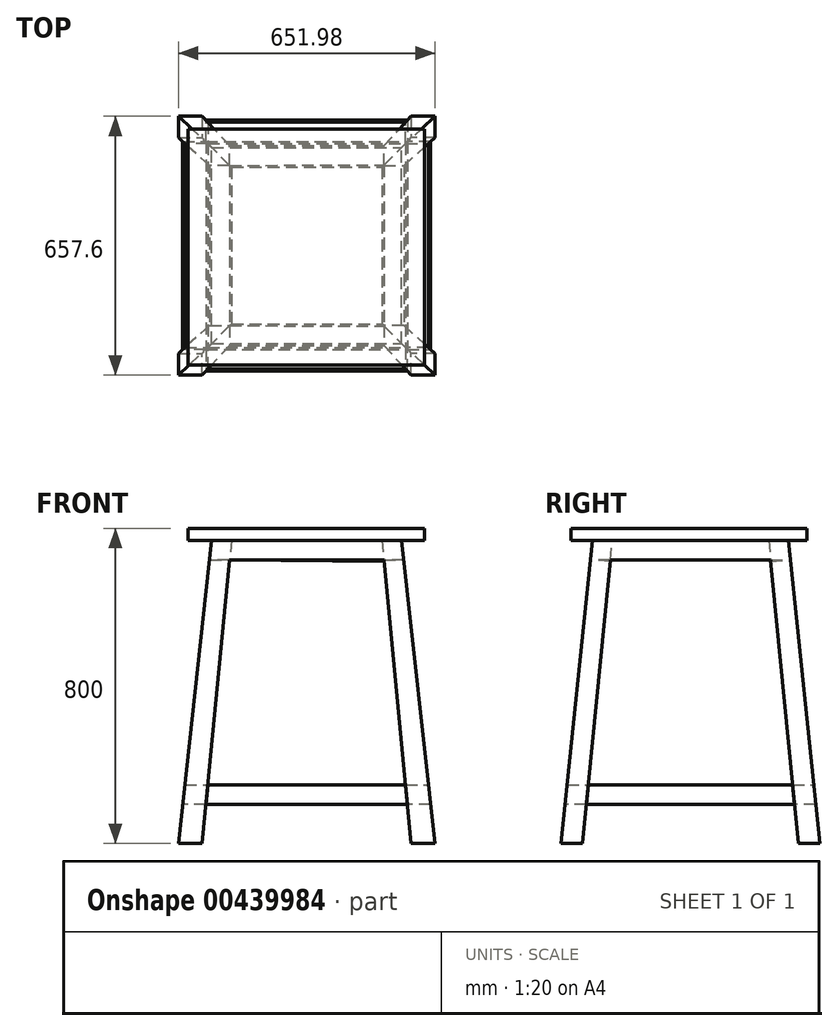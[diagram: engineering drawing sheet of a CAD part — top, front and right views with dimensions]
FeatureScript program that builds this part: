
annotation { "Feature Type Name" : "Feature", "Feature Type Description" : "" }
export const myFeature = defineFeature(function(context is Context, id is Id, definition is map)
    precondition{}
    {
        {
            var Q0;
            Q0=qCreatedBy(makeId("Top.planeOp"),FACE);
            var sketch = newSketch(context, id + "F0", { "sketchPlane" : qUnion([Q0])});
            skLineSegment(sketch, "E0.bottom", {"start": v(-301, 296.2) * mm, "end": v(299, 296.2) * mm});
            skLineSegment(sketch, "E0.top", {"start": v(-301, -303.8) * mm, "end": v(299, -303.8) * mm});
            skLineSegment(sketch, "E0.left", {"start": v(-301, 296.2) * mm, "end": v(-301, -303.8) * mm});
            skLineSegment(sketch, "E0.right", {"start": v(299, 296.2) * mm, "end": v(299, -303.8) * mm});
            skSolve(sketch);
        }
        {
            var Q0;
            Q0 = qSketchRegion(id + "F0", true);
            extrude(context, id + "F1", {"entities" : qUnion([Q0]), "depth" : 30 * mm});
        }
        {
            var Q0;
            Q0=qCreatedBy(makeId("Top.planeOp"),FACE);
            var sketch = newSketch(context, id + "F2", { "sketchPlane" : qUnion([Q0])});
            skLineSegment(sketch, "E1.bottom", {"start": v(-241.24, -248.9) * mm, "end": v(-191.24, -248.9) * mm});
            skLineSegment(sketch, "E1.top", {"start": v(-241.24, -198.9) * mm, "end": v(-191.24, -198.9) * mm});
            skLineSegment(sketch, "E1.left", {"start": v(-241.24, -248.9) * mm, "end": v(-241.24, -198.9) * mm});
            skLineSegment(sketch, "E1.right", {"start": v(-191.24, -248.9) * mm, "end": v(-191.24, -198.9) * mm});
            skSolve(sketch);
        }
        {
            var Q0;
            Q0=makeQuery(id+"F1.opExtrude","CAP_FACE",FACE,{"disambiguationData":[OSD([sQuery(id+"F0.wireOp",EDGE,"E0.bottom"),sQuery(id+"F0.wireOp",EDGE,"E0.top"),sQuery(id+"F0.wireOp",EDGE,"E0.left"),sQuery(id+"F0.wireOp",EDGE,"E0.right")])],"isStart":false});
            cPlane(context, id + "F3", {"entities" : qUnion([Q0]), "cplaneType" : CPlaneType.OFFSET, "offset" : 800 * mm, "oppositeDirection" : true, "width" : 150 * mm, "height" : 150 * mm});
        }
        {
            var Q0;
            Q0=qCreatedBy(id+"F3.planeOp",FACE);
            var sketch = newSketch(context, id + "F4", { "sketchPlane" : qUnion([Q0])});
            skLineSegment(sketch, "E2.bottom", {"start": v(-326, -328.8) * mm, "end": v(-265.45, -328.8) * mm});
            skLineSegment(sketch, "E2.top", {"start": v(-326, -273.84) * mm, "end": v(-265.45, -273.84) * mm});
            skLineSegment(sketch, "E2.left", {"start": v(-326, -328.8) * mm, "end": v(-326, -273.84) * mm});
            skLineSegment(sketch, "E2.right", {"start": v(-265.45, -328.8) * mm, "end": v(-265.45, -273.84) * mm});
            skSolve(sketch);
        }
        {
            var Q1;
            Q1=makeQuery(id+"F2.imprint","IMPRINT",FACE,{"disambiguationData":[TD([[makeQuery(id+"F2.imprint","IMPRINT",EDGE,{"derivedFrom":sQuery(id+"F2.wireOp",EDGE,"E1.bottom")}),1.0]])]});
            var Q2;
            Q2=makeQuery(id+"F4.imprint","IMPRINT",FACE,{"disambiguationData":[TD([[makeQuery(id+"F4.imprint","IMPRINT",EDGE,{"derivedFrom":sQuery(id+"F4.wireOp",EDGE,"E2.bottom")}),1.0]])]});
            loft(context, id + "F5", {"sheetProfilesArray" : [{ "sheetProfileEntities" : qUnion([Q1]) }, { "sheetProfileEntities" : qUnion([Q2]) }]});
        }
        {
            var Q0;
            Q0=makeQuery(id+"F5.opLoft","SWEPT_BODY",BODY,{"disambiguationData":[OSD([makeQuery(id+"F2.imprint","IMPRINT",FACE,{"disambiguationData":[TD([[makeQuery(id+"F2.imprint","IMPRINT",EDGE,{"derivedFrom":sQuery(id+"F2.wireOp",EDGE,"E1.bottom")}),1.0]])]}),makeQuery(id+"F4.imprint","IMPRINT",FACE,{"disambiguationData":[TD([[makeQuery(id+"F4.imprint","IMPRINT",EDGE,{"derivedFrom":sQuery(id+"F4.wireOp",EDGE,"E2.bottom")}),1.0]])]})])]});
            var Q1;
            Q1=qCreatedBy(makeId("Right.planeOp"),FACE);
            mirror(context, id + "F6", {"entities" : qUnion([Q0]), "mirrorPlane" : qUnion([Q1])});
        }
        {
            var Q0;
            Q0=makeQuery(id+"F6.opPattern","COPY",BODY,{"derivedFrom":makeQuery(id+"F5.opLoft","SWEPT_BODY",BODY,{"disambiguationData":[OSD([makeQuery(id+"F2.imprint","IMPRINT",FACE,{"disambiguationData":[TD([[makeQuery(id+"F2.imprint","IMPRINT",EDGE,{"derivedFrom":sQuery(id+"F2.wireOp",EDGE,"E1.bottom")}),1.0]])]}),makeQuery(id+"F4.imprint","IMPRINT",FACE,{"disambiguationData":[TD([[makeQuery(id+"F4.imprint","IMPRINT",EDGE,{"derivedFrom":sQuery(id+"F4.wireOp",EDGE,"E2.bottom")}),1.0]])]})])]}),"instanceName":"1"});
            var Q1;
            Q1=makeQuery(id+"F5.opLoft","SWEPT_BODY",BODY,{"disambiguationData":[OSD([makeQuery(id+"F2.imprint","IMPRINT",FACE,{"disambiguationData":[TD([[makeQuery(id+"F2.imprint","IMPRINT",EDGE,{"derivedFrom":sQuery(id+"F2.wireOp",EDGE,"E1.bottom")}),1.0]])]}),makeQuery(id+"F4.imprint","IMPRINT",FACE,{"disambiguationData":[TD([[makeQuery(id+"F4.imprint","IMPRINT",EDGE,{"derivedFrom":sQuery(id+"F4.wireOp",EDGE,"E2.bottom")}),1.0]])]})])]});
            var Q2;
            Q2=qCreatedBy(makeId("Front.planeOp"),FACE);
            mirror(context, id + "F7", {"operationType" : NewBodyOperationType.ADD, "entities" : qUnion([Q0, Q1]), "mirrorPlane" : qUnion([Q2])});
        }
        {
            var Q0;
            Q0=makeQuery(id+"F7.opPattern","COPY",FACE,{"derivedFrom":makeQuery(id+"F6.opPattern","COPY",FACE,{"derivedFrom":makeQuery(id+"F5.opLoft","SWEPT_FACE",FACE,{"disambiguationData":[OSD([sQuery(id+"F2.wireOp",EDGE,"E1.bottom"),sQuery(id+"F2.wireOp",EDGE,"E1.top"),sQuery(id+"F2.wireOp",EDGE,"E1.right"),sQuery(id+"F4.wireOp",EDGE,"E2.bottom"),sQuery(id+"F4.wireOp",EDGE,"E2.top"),sQuery(id+"F4.wireOp",EDGE,"E2.right")])]}),"instanceName":"1"}),"instanceName":"1"});
            var sketch = newSketch(context, id + "F8", { "sketchPlane" : qUnion([Q0])});
            skLineSegment(sketch, "E3", {"start": v(-318.47, -691.91) * mm, "end": v(-264.15, -691.91) * mm});
            skLineSegment(sketch, "E4", {"start": v(-264.15, -691.91) * mm, "end": v(-259.33, -642.18) * mm});
            skLineSegment(sketch, "E5", {"start": v(-259.33, -642.18) * mm, "end": v(-313.34, -642.18) * mm});
            skLineSegment(sketch, "E6", {"start": v(-313.34, -642.18) * mm, "end": v(-318.47, -691.91) * mm});
            skSolve(sketch);
        }
        {
            var Q0;
            Q0=makeQuery(id+"F7.opPattern","COPY",FACE,{"derivedFrom":makeQuery(id+"F5.opLoft","SWEPT_FACE",FACE,{"disambiguationData":[OSD([sQuery(id+"F2.wireOp",EDGE,"E1.bottom"),sQuery(id+"F2.wireOp",EDGE,"E1.top"),sQuery(id+"F2.wireOp",EDGE,"E1.right"),sQuery(id+"F4.wireOp",EDGE,"E2.bottom"),sQuery(id+"F4.wireOp",EDGE,"E2.top"),sQuery(id+"F4.wireOp",EDGE,"E2.right")])]}),"instanceName":"1"});
            var sketch = newSketch(context, id + "F9", { "sketchPlane" : qUnion([Q0])});
            skLineSegment(sketch, "E7", {"start": v(264.15, -691.91) * mm, "end": v(318.47, -691.91) * mm});
            skLineSegment(sketch, "E8", {"start": v(318.47, -691.91) * mm, "end": v(313.34, -642.18) * mm});
            skLineSegment(sketch, "E9", {"start": v(313.34, -642.18) * mm, "end": v(259.33, -642.18) * mm});
            skLineSegment(sketch, "E10", {"start": v(259.33, -642.18) * mm, "end": v(264.15, -691.91) * mm});
            skSolve(sketch);
        }
        {
            var Q1;
            Q1=makeQuery(id+"F9.imprint","IMPRINT",FACE,{"disambiguationData":[TD([[makeQuery(id+"F9.imprint","IMPRINT",EDGE,{"derivedFrom":sQuery(id+"F9.wireOp",EDGE,"E7")}),1.0]])]});
            var Q2;
            Q2=makeQuery(id+"F8.imprint","IMPRINT",FACE,{"disambiguationData":[TD([[makeQuery(id+"F8.imprint","IMPRINT",EDGE,{"derivedFrom":sQuery(id+"F8.wireOp",EDGE,"E3")}),1.0]])]});
            loft(context, id + "F10", {"sheetProfilesArray" : [{ "sheetProfileEntities" : qUnion([Q1]) }, { "sheetProfileEntities" : qUnion([Q2]) }]});
        }
        {
            var Q0;
            Q0=makeQuery(id+"F10.opLoft","SWEPT_BODY",BODY,{"disambiguationData":[OSD([makeQuery(id+"F8.imprint","IMPRINT",FACE,{"disambiguationData":[TD([[makeQuery(id+"F8.imprint","IMPRINT",EDGE,{"derivedFrom":sQuery(id+"F8.wireOp",EDGE,"E3")}),1.0]])]}),makeQuery(id+"F9.imprint","IMPRINT",FACE,{"disambiguationData":[TD([[makeQuery(id+"F9.imprint","IMPRINT",EDGE,{"derivedFrom":sQuery(id+"F9.wireOp",EDGE,"E7")}),1.0]])]})])]});
            var Q1;
            Q1=qCreatedBy(makeId("Front.planeOp"),FACE);
            mirror(context, id + "F11", {"entities" : qUnion([Q0]), "mirrorPlane" : qUnion([Q1])});
        }
        {
            var Q0;
            Q0=makeQuery(id+"F5.opLoft","SWEPT_FACE",FACE,{"disambiguationData":[OSD([sQuery(id+"F2.wireOp",EDGE,"E1.top"),sQuery(id+"F2.wireOp",EDGE,"E1.left"),sQuery(id+"F2.wireOp",EDGE,"E1.right"),sQuery(id+"F4.wireOp",EDGE,"E2.top"),sQuery(id+"F4.wireOp",EDGE,"E2.left"),sQuery(id+"F4.wireOp",EDGE,"E2.right")])]});
            var sketch = newSketch(context, id + "F12", { "sketchPlane" : qUnion([Q0])});
            skLineSegment(sketch, "E11", {"start": v(255.85, -692.9) * mm, "end": v(315.04, -692.9) * mm});
            skLineSegment(sketch, "E12", {"start": v(315.04, -692.9) * mm, "end": v(309.6, -643.2) * mm});
            skLineSegment(sketch, "E13", {"start": v(309.6, -643.2) * mm, "end": v(251.09, -643.2) * mm});
            skLineSegment(sketch, "E14", {"start": v(251.09, -643.2) * mm, "end": v(255.85, -692.9) * mm});
            skSolve(sketch);
        }
        {
            var Q0;
            Q0=makeQuery(id+"F7.opPattern","COPY",FACE,{"derivedFrom":makeQuery(id+"F5.opLoft","SWEPT_FACE",FACE,{"disambiguationData":[OSD([sQuery(id+"F2.wireOp",EDGE,"E1.top"),sQuery(id+"F2.wireOp",EDGE,"E1.left"),sQuery(id+"F2.wireOp",EDGE,"E1.right"),sQuery(id+"F4.wireOp",EDGE,"E2.top"),sQuery(id+"F4.wireOp",EDGE,"E2.left"),sQuery(id+"F4.wireOp",EDGE,"E2.right")])]}),"instanceName":"1"});
            var sketch = newSketch(context, id + "F13", { "sketchPlane" : qUnion([Q0])});
            skLineSegment(sketch, "E15", {"start": v(-251.09, -643.2) * mm, "end": v(-309.6, -643.2) * mm});
            skLineSegment(sketch, "E16", {"start": v(-309.6, -643.2) * mm, "end": v(-315.04, -692.9) * mm});
            skLineSegment(sketch, "E17", {"start": v(-315.04, -692.9) * mm, "end": v(-255.85, -692.9) * mm});
            skLineSegment(sketch, "E18", {"start": v(-255.85, -692.9) * mm, "end": v(-251.09, -643.2) * mm});
            skSolve(sketch);
        }
        {
            var Q1;
            Q1=makeQuery(id+"F13.imprint","IMPRINT",FACE,{"disambiguationData":[TD([[makeQuery(id+"F13.imprint","IMPRINT",EDGE,{"derivedFrom":sQuery(id+"F13.wireOp",EDGE,"E15")}),1.0]])]});
            var Q2;
            Q2=makeQuery(id+"F12.imprint","IMPRINT",FACE,{"disambiguationData":[TD([[makeQuery(id+"F12.imprint","IMPRINT",EDGE,{"derivedFrom":sQuery(id+"F12.wireOp",EDGE,"E11")}),1.0]])]});
            loft(context, id + "F14", {"sheetProfilesArray" : [{ "sheetProfileEntities" : qUnion([Q1]) }, { "sheetProfileEntities" : qUnion([Q2]) }]});
        }
        {
            var Q0;
            Q0=makeQuery(id+"F14.opLoft","SWEPT_BODY",BODY,{"disambiguationData":[OSD([makeQuery(id+"F12.imprint","IMPRINT",FACE,{"disambiguationData":[TD([[makeQuery(id+"F12.imprint","IMPRINT",EDGE,{"derivedFrom":sQuery(id+"F12.wireOp",EDGE,"E11")}),1.0]])]}),makeQuery(id+"F13.imprint","IMPRINT",FACE,{"disambiguationData":[TD([[makeQuery(id+"F13.imprint","IMPRINT",EDGE,{"derivedFrom":sQuery(id+"F13.wireOp",EDGE,"E15")}),1.0]])]})])]});
            var Q1;
            Q1=qCreatedBy(makeId("Right.planeOp"),FACE);
            mirror(context, id + "F15", {"entities" : qUnion([Q0]), "mirrorPlane" : qUnion([Q1])});
        }
        {
            var Q0;
            Q0=makeQuery(id+"F7.opPattern","COPY",FACE,{"derivedFrom":makeQuery(id+"F6.opPattern","COPY",FACE,{"derivedFrom":makeQuery(id+"F5.opLoft","SWEPT_FACE",FACE,{"disambiguationData":[OSD([sQuery(id+"F2.wireOp",EDGE,"E1.bottom"),sQuery(id+"F2.wireOp",EDGE,"E1.top"),sQuery(id+"F2.wireOp",EDGE,"E1.right"),sQuery(id+"F4.wireOp",EDGE,"E2.bottom"),sQuery(id+"F4.wireOp",EDGE,"E2.top"),sQuery(id+"F4.wireOp",EDGE,"E2.right")])]}),"instanceName":"1"}),"instanceName":"1"});
            var sketch = newSketch(context, id + "F16", { "sketchPlane" : qUnion([Q0])});
            skLineSegment(sketch, "E19", {"start": v(-248.9, -18.35) * mm, "end": v(-198.9, -18.35) * mm});
            skLineSegment(sketch, "E20", {"start": v(-198.9, -18.35) * mm, "end": v(-204.18, -72.91) * mm});
            skLineSegment(sketch, "E21", {"start": v(-204.18, -72.91) * mm, "end": v(-254.03, -68.08) * mm});
            skLineSegment(sketch, "E22", {"start": v(-254.03, -68.08) * mm, "end": v(-248.9, -18.35) * mm});
            skSolve(sketch);
        }
        {
            var Q0;
            Q0=makeQuery(id+"F7.opPattern","COPY",FACE,{"derivedFrom":makeQuery(id+"F5.opLoft","SWEPT_FACE",FACE,{"disambiguationData":[OSD([sQuery(id+"F2.wireOp",EDGE,"E1.bottom"),sQuery(id+"F2.wireOp",EDGE,"E1.top"),sQuery(id+"F2.wireOp",EDGE,"E1.right"),sQuery(id+"F4.wireOp",EDGE,"E2.bottom"),sQuery(id+"F4.wireOp",EDGE,"E2.top"),sQuery(id+"F4.wireOp",EDGE,"E2.right")])]}),"instanceName":"1"});
            var sketch = newSketch(context, id + "F17", { "sketchPlane" : qUnion([Q0])});
            skLineSegment(sketch, "E23", {"start": v(248.9, -18.35) * mm, "end": v(198.9, -18.35) * mm});
            skLineSegment(sketch, "E24", {"start": v(198.9, -18.35) * mm, "end": v(203.71, -68.08) * mm});
            skLineSegment(sketch, "E25", {"start": v(203.71, -68.08) * mm, "end": v(254.03, -68.08) * mm});
            skLineSegment(sketch, "E26", {"start": v(254.03, -68.08) * mm, "end": v(248.9, -18.35) * mm});
            skSolve(sketch);
        }
        {
            var Q1;
            Q1=makeQuery(id+"F17.imprint","IMPRINT",FACE,{"disambiguationData":[TD([[makeQuery(id+"F17.imprint","IMPRINT",EDGE,{"derivedFrom":sQuery(id+"F17.wireOp",EDGE,"E23")}),-1.0]])]});
            var Q2;
            Q2=makeQuery(id+"F16.imprint","IMPRINT",FACE,{"disambiguationData":[TD([[makeQuery(id+"F16.imprint","IMPRINT",EDGE,{"derivedFrom":sQuery(id+"F16.wireOp",EDGE,"E19")}),1.0]])]});
            loft(context, id + "F18", {"sheetProfilesArray" : [{ "sheetProfileEntities" : qUnion([Q1]) }, { "sheetProfileEntities" : qUnion([Q2]) }]});
        }
        {
            var Q0;
            Q0=makeQuery(id+"F18.opLoft","SWEPT_BODY",BODY,{"disambiguationData":[OSD([makeQuery(id+"F16.imprint","IMPRINT",FACE,{"disambiguationData":[TD([[makeQuery(id+"F16.imprint","IMPRINT",EDGE,{"derivedFrom":sQuery(id+"F16.wireOp",EDGE,"E19")}),1.0]])]}),makeQuery(id+"F17.imprint","IMPRINT",FACE,{"disambiguationData":[TD([[makeQuery(id+"F17.imprint","IMPRINT",EDGE,{"derivedFrom":sQuery(id+"F17.wireOp",EDGE,"E23")}),-1.0]])]})])]});
            var Q1;
            Q1=qCreatedBy(makeId("Front.planeOp"),FACE);
            mirror(context, id + "F19", {"operationType" : NewBodyOperationType.ADD, "entities" : qUnion([Q0]), "mirrorPlane" : qUnion([Q1])});
        }
        {
            var Q0;
            {var subQ0=sQuery(id+"F4.wireOp",EDGE,"E2.right");var subQ1=sQuery(id+"F4.wireOp",EDGE,"E2.top");var subQ2=sQuery(id+"F2.wireOp",EDGE,"E1.right");var subQ3=sQuery(id+"F2.wireOp",EDGE,"E1.top");var subQ4=makeQuery(id+"F5.opLoft","SWEPT_FACE",FACE,{"disambiguationData":[OSD([subQ3,sQuery(id+"F2.wireOp",EDGE,"E1.left"),subQ2,subQ1,sQuery(id+"F4.wireOp",EDGE,"E2.left"),subQ0])]});Q0=makeQuery(id+"F19.boolean.opBoolean","MERGE",FACE,{"derivedFrom":[subQ4,makeQuery(id+"F6.opPattern","COPY",FACE,{"derivedFrom":subQ4,"instanceName":"1"}),makeQuery(id+"F19.opPattern","COPY",FACE,{"derivedFrom":makeQuery(id+"F18.opLoft","SWEPT_FACE",FACE,{"disambiguationData":[OSD([subQ3,subQ2,subQ1,subQ0,sQuery(id+"F16.wireOp",EDGE,"E19"),sQuery(id+"F16.wireOp",EDGE,"E20"),sQuery(id+"F16.wireOp",EDGE,"E21"),sQuery(id+"F17.wireOp",EDGE,"E23"),sQuery(id+"F17.wireOp",EDGE,"E24"),sQuery(id+"F17.wireOp",EDGE,"E25")])]}),"instanceName":"1"})]});}
            var sketch = newSketch(context, id + "F20", { "sketchPlane" : qUnion([Q0])});
            skLineSegment(sketch, "E27", {"start": v(190.91, -19.27) * mm, "end": v(241.24, -19.27) * mm});
            skLineSegment(sketch, "E28", {"start": v(241.24, -19.27) * mm, "end": v(246.68, -68.97) * mm});
            skLineSegment(sketch, "E29", {"start": v(246.68, -68.97) * mm, "end": v(196, -69) * mm});
            skLineSegment(sketch, "E30", {"start": v(196, -69) * mm, "end": v(190.91, -19.27) * mm});
            skSolve(sketch);
        }
        {
            var Q0;
            {var subQ0=sQuery(id+"F4.wireOp",EDGE,"E2.right");var subQ1=sQuery(id+"F4.wireOp",EDGE,"E2.top");var subQ2=sQuery(id+"F2.wireOp",EDGE,"E1.right");var subQ3=sQuery(id+"F2.wireOp",EDGE,"E1.top");var subQ4=makeQuery(id+"F5.opLoft","SWEPT_FACE",FACE,{"disambiguationData":[OSD([subQ3,sQuery(id+"F2.wireOp",EDGE,"E1.left"),subQ2,subQ1,sQuery(id+"F4.wireOp",EDGE,"E2.left"),subQ0])]});Q0=makeQuery(id+"F19.boolean.opBoolean","MERGE",FACE,{"derivedFrom":[makeQuery(id+"F7.opPattern","COPY",FACE,{"derivedFrom":subQ4,"instanceName":"1"}),makeQuery(id+"F7.opPattern","COPY",FACE,{"derivedFrom":makeQuery(id+"F6.opPattern","COPY",FACE,{"derivedFrom":subQ4,"instanceName":"1"}),"instanceName":"1"}),makeQuery(id+"F18.opLoft","SWEPT_FACE",FACE,{"disambiguationData":[OSD([subQ3,subQ2,subQ1,subQ0,sQuery(id+"F16.wireOp",EDGE,"E19"),sQuery(id+"F16.wireOp",EDGE,"E20"),sQuery(id+"F16.wireOp",EDGE,"E21"),sQuery(id+"F17.wireOp",EDGE,"E23"),sQuery(id+"F17.wireOp",EDGE,"E24"),sQuery(id+"F17.wireOp",EDGE,"E25")])]})]});}
            var sketch = newSketch(context, id + "F21", { "sketchPlane" : qUnion([Q0])});
            skLineSegment(sketch, "E31", {"start": v(-241.24, -19.27) * mm, "end": v(-190.91, -19.27) * mm});
            skLineSegment(sketch, "E32", {"start": v(-190.91, -19.27) * mm, "end": v(-196, -69) * mm});
            skLineSegment(sketch, "E33", {"start": v(-196, -69) * mm, "end": v(-246.68, -69) * mm});
            skLineSegment(sketch, "E34", {"start": v(-246.68, -69) * mm, "end": v(-241.24, -19.27) * mm});
            skSolve(sketch);
        }
        {
            var Q1;
            Q1=makeQuery(id+"F21.imprint","IMPRINT",FACE,{"disambiguationData":[TD([[makeQuery(id+"F21.imprint","IMPRINT",EDGE,{"derivedFrom":sQuery(id+"F21.wireOp",EDGE,"E31")}),-1.0]])]});
            var Q2;
            Q2=makeQuery(id+"F20.imprint","IMPRINT",FACE,{"disambiguationData":[TD([[makeQuery(id+"F20.imprint","IMPRINT",EDGE,{"derivedFrom":sQuery(id+"F20.wireOp",EDGE,"E27")}),1.0]])]});
            loft(context, id + "F22", {"sheetProfilesArray" : [{ "sheetProfileEntities" : qUnion([Q1]) }, { "sheetProfileEntities" : qUnion([Q2]) }]});
        }
        {
            var Q0;
            Q0=makeQuery(id+"F22.opLoft","SWEPT_BODY",BODY,{"disambiguationData":[OSD([makeQuery(id+"F20.imprint","IMPRINT",FACE,{"disambiguationData":[TD([[makeQuery(id+"F20.imprint","IMPRINT",EDGE,{"derivedFrom":sQuery(id+"F20.wireOp",EDGE,"E27")}),1.0]])]}),makeQuery(id+"F21.imprint","IMPRINT",FACE,{"disambiguationData":[TD([[makeQuery(id+"F21.imprint","IMPRINT",EDGE,{"derivedFrom":sQuery(id+"F21.wireOp",EDGE,"E31")}),-1.0]])]})])]});
            var Q1;
            Q1=qCreatedBy(makeId("Right.planeOp"),FACE);
            mirror(context, id + "F23", {"operationType" : NewBodyOperationType.ADD, "entities" : qUnion([Q0]), "mirrorPlane" : qUnion([Q1])});
        }
    });
